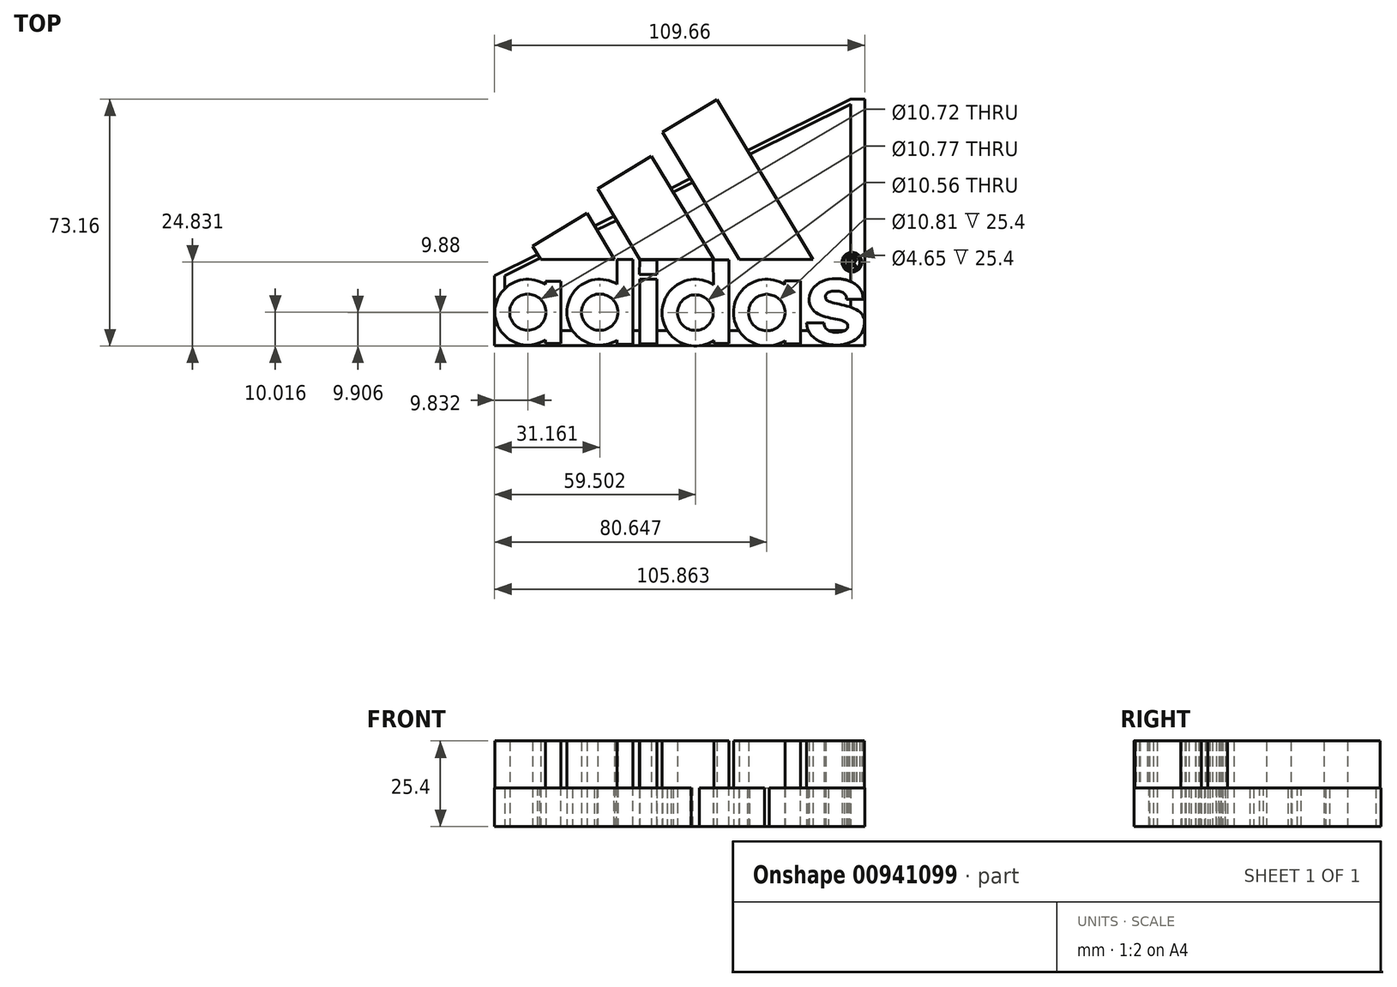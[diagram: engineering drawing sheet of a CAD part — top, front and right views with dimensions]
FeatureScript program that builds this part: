
annotation { "Feature Type Name" : "Feature", "Feature Type Description" : "" }
export const myFeature = defineFeature(function(context is Context, id is Id, definition is map)
    precondition{}
    {
        {
            var Q0;
            Q0=qCreatedBy(makeId("Top.planeOp"),FACE);
            var sketch = newSketch(context, id + "F0", { "sketchPlane" : qUnion([Q0])});
            skLineSegment(sketch, "E0", {"start": v(-48.12, -6.63) * mm, "end": v(-45.76, -10.62) * mm});
            skLineSegment(sketch, "E1", {"start": v(-45.76, -10.62) * mm, "end": v(-23.92, -10.62) * mm});
            skLineSegment(sketch, "E2", {"start": v(-23.92, -10.62) * mm, "end": v(-32.06, 3.04) * mm});
            skLineSegment(sketch, "E3", {"start": v(-32.06, 3.04) * mm, "end": v(-48.12, -6.63) * mm});
            skLineSegment(sketch, "E4", {"start": v(-28.86, 10.33) * mm, "end": v(-16.43, -10.57) * mm});
            skLineSegment(sketch, "E5", {"start": v(-16.43, -10.57) * mm, "end": v(5.51, -10.57) * mm});
            skLineSegment(sketch, "E6", {"start": v(5.51, -10.57) * mm, "end": v(-12.92, 20) * mm});
            skLineSegment(sketch, "E7", {"start": v(-12.92, 20) * mm, "end": v(-28.86, 10.33) * mm});
            skLineSegment(sketch, "E8", {"start": v(13, -10.63) * mm, "end": v(34.92, -10.63) * mm});
            skLineSegment(sketch, "E9", {"start": v(34.92, -10.63) * mm, "end": v(6.4, 36.7) * mm});
            skLineSegment(sketch, "E10", {"start": v(6.4, 36.7) * mm, "end": v(-9.65, 27.04) * mm});
            skLineSegment(sketch, "E11", {"start": v(-9.65, 27.04) * mm, "end": v(13, -10.63) * mm});
            skLineSegment(sketch, "E12", {"start": v(-44.36, -17.06) * mm, "end": v(-39.82, -17.06) * mm});
            skLineSegment(sketch, "E13", {"start": v(-39.82, -17.06) * mm, "end": v(-39.82, -35.56) * mm});
            skLineSegment(sketch, "E14", {"start": v(-39.82, -35.56) * mm, "end": v(-44.36, -35.56) * mm});
            skLineSegment(sketch, "E15", {"start": v(-23.11, -10.57) * mm, "end": v(-18.48, -10.57) * mm});
            skLineSegment(sketch, "E16", {"start": v(-18.48, -10.57) * mm, "end": v(-18.48, -35.72) * mm});
            skLineSegment(sketch, "E17", {"start": v(-18.48, -35.72) * mm, "end": v(-23.07, -35.72) * mm});
            skCircle(sketch, "E18", {"center": v(-49.58, -26.25) * mm, "radius": 9.74 * mm});
            skCircle(sketch, "E19", {"center": v(-28.25, -26.25) * mm, "radius": 9.75 * mm});
            skCircle(sketch, "E20", {"center": v(0.1, -26.39) * mm, "radius": 9.88 * mm});
            skCircle(sketch, "E21", {"center": v(21.24, -26.36) * mm, "radius": 9.86 * mm});
            skLineSegment(sketch, "E22", {"start": v(-16.48, -15.1) * mm, "end": v(-11.34, -15.1) * mm});
            skLineSegment(sketch, "E23", {"start": v(-11.34, -15.1) * mm, "end": v(-11.34, -10.8) * mm});
            skLineSegment(sketch, "E24", {"start": v(-11.34, -10.8) * mm, "end": v(-16.45, -10.8) * mm});
            skLineSegment(sketch, "E25", {"start": v(-16.45, -10.8) * mm, "end": v(-16.48, -15.1) * mm});
            skLineSegment(sketch, "E26", {"start": v(-16.37, -16.5) * mm, "end": v(-11.37, -16.5) * mm});
            skLineSegment(sketch, "E27", {"start": v(-11.37, -16.5) * mm, "end": v(-11.37, -35.62) * mm});
            skLineSegment(sketch, "E28", {"start": v(-11.37, -35.62) * mm, "end": v(-16.35, -35.62) * mm});
            skLineSegment(sketch, "E29", {"start": v(-16.35, -35.62) * mm, "end": v(-16.37, -16.5) * mm});
            skLineSegment(sketch, "E30", {"start": v(5.37, -10.76) * mm, "end": v(10.03, -10.76) * mm});
            skLineSegment(sketch, "E31", {"start": v(10.03, -10.76) * mm, "end": v(10.03, -35.57) * mm});
            skLineSegment(sketch, "E32", {"start": v(10.03, -35.57) * mm, "end": v(5.51, -35.57) * mm});
            skLineSegment(sketch, "E33", {"start": v(26.55, -17.03) * mm, "end": v(31.2, -17.03) * mm});
            skLineSegment(sketch, "E34", {"start": v(31.2, -17.03) * mm, "end": v(31.2, -35.6) * mm});
            skLineSegment(sketch, "E35", {"start": v(31.2, -35.6) * mm, "end": v(26.62, -35.6) * mm});
            skCircle(sketch, "E36", {"center": v(-49.58, -26.25) * mm, "radius": 5.36 * mm});
            skCircle(sketch, "E37", {"center": v(-28.25, -26.25) * mm, "radius": 5.39 * mm});
            skCircle(sketch, "E38", {"center": v(0.1, -26.39) * mm, "radius": 5.28 * mm});
            skCircle(sketch, "E39", {"center": v(21.24, -26.36) * mm, "radius": 5.4 * mm});
            skLineSegment(sketch, "E40", {"start": v(-44.36, -35.56) * mm, "end": v(-44.36, -17.06) * mm});
            skLineSegment(sketch, "E41", {"start": v(-23.07, -35.72) * mm, "end": v(-23.11, -10.57) * mm});
            skLineSegment(sketch, "E42", {"start": v(5.51, -35.57) * mm, "end": v(5.37, -10.76) * mm});
            skLineSegment(sketch, "E43", {"start": v(26.55, -17.03) * mm, "end": v(26.62, -35.6) * mm});
            skCircle(sketch, "E44", {"center": v(46.45, -11.44) * mm, "radius": 2.92 * mm});
            skCircle(sketch, "E45", {"center": v(46.45, -11.44) * mm, "radius": 2.33 * mm});
            skFitSpline(sketch, "E46", {"points": [v(49.72, -22.41) * mm, v(33.72, -22.3) * mm], "startDerivative": vector(1.34, 22.95) * mm, "endDerivative": vector(-2.06, -25.44) * mm});
            skFitSpline(sketch, "E47", {"points": [v(33.72, -22.3) * mm, v(45.18, -30.56) * mm], "startDerivative": vector(0.87, -23.1) * mm, "endDerivative": vector(-1.17, -11.35) * mm});
            skFitSpline(sketch, "E48", {"points": [v(38.16, -29.4) * mm, v(45.18, -30.56) * mm], "startDerivative": vector(0.07, -12.28) * mm, "endDerivative": vector(-0.36, 5.8) * mm});
            skFitSpline(sketch, "E49", {"points": [v(33.03, -29.41) * mm, v(50.17, -29.38) * mm], "startDerivative": vector(0.17, -25.21) * mm, "endDerivative": vector(0.56, 27.5) * mm});
            skFitSpline(sketch, "E50", {"points": [v(50.17, -29.38) * mm, v(38.67, -22.07) * mm], "startDerivative": vector(0.52, 18.6) * mm, "endDerivative": vector(-0.45, 7.35) * mm});
            skFitSpline(sketch, "E51", {"points": [v(38.67, -22.07) * mm, v(44.77, -22.07) * mm], "startDerivative": vector(-2.36, 8.49) * mm, "endDerivative": vector(-0.86, -8.34) * mm});
            skLineSegment(sketch, "E52", {"start": v(33.03, -29.41) * mm, "end": v(38.16, -29.4) * mm});
            skLineSegment(sketch, "E53", {"start": v(49.72, -22.41) * mm, "end": v(44.77, -22.41) * mm});
            skLineSegment(sketch, "E54", {"start": v(44.77, -22.41) * mm, "end": v(44.77, -22.07) * mm});
            skLineSegment(sketch, "E55.bottom", {"start": v(45.7, -13.01) * mm, "end": v(45.16, -13.01) * mm});
            skLineSegment(sketch, "E55.top", {"start": v(45.7, -9.92) * mm, "end": v(45.16, -9.92) * mm});
            skLineSegment(sketch, "E55.left", {"start": v(45.7, -13.01) * mm, "end": v(45.7, -9.92) * mm});
            skLineSegment(sketch, "E55.right", {"start": v(45.16, -13.01) * mm, "end": v(45.16, -9.92) * mm});
            skLineSegment(sketch, "E56", {"start": v(45.7, -9.92) * mm, "end": v(47.02, -9.92) * mm});
            skLineSegment(sketch, "E57", {"start": v(45.7, -11.78) * mm, "end": v(46.41, -11.78) * mm});
            skLineSegment(sketch, "E58", {"start": v(46.41, -11.78) * mm, "end": v(47.15, -12.94) * mm});
            skLineSegment(sketch, "E59", {"start": v(47.15, -12.94) * mm, "end": v(47.85, -12.94) * mm});
            skLineSegment(sketch, "E60", {"start": v(47.85, -12.94) * mm, "end": v(47.05, -11.78) * mm});
            skLineSegment(sketch, "E61", {"start": v(47.05, -11.78) * mm, "end": v(46.83, -11.78) * mm});
            skFitSpline(sketch, "E62", {"points": [v(46.83, -11.78) * mm, v(47.02, -9.92) * mm], "startDerivative": vector(-0.66, 0.48) * mm, "endDerivative": vector(-5.18, 3.5) * mm});
            skLineSegment(sketch, "E63", {"start": v(45.7, -10.48) * mm, "end": v(46.8, -10.48) * mm});
            skLineSegment(sketch, "E64", {"start": v(45.7, -11.11) * mm, "end": v(46.8, -11.11) * mm});
            skFitSpline(sketch, "E65", {"points": [v(46.8, -10.48) * mm, v(46.8, -11.11) * mm], "startDerivative": vector(1.32, -1.07) * mm, "endDerivative": vector(-0.32, -0.18) * mm});
            skSolve(sketch);
        }
        {
            var Q0;
            {var subQ0=sQuery(id+"F0.wireOp",EDGE,"E40");var subQ1=sQuery(id+"F0.wireOp",EDGE,"E18");var subQ2=makeQuery(id+"F0.imprint","INTERSECT",VERTEX,{"disambiguationData":[OD(0.0)],"derivedFrom":[subQ1,subQ0]});Q0=makeQuery(id+"F0.imprint","IMPRINT",FACE,{"disambiguationData":[TD([[makeQuery(id+"F0.imprint","IMPRINT",EDGE,{"disambiguationData":[TD([[subQ2,1.0]])],"derivedFrom":subQ1}),1.0]])]});}
            var Q1;
            {var subQ0=sQuery(id+"F0.wireOp",EDGE,"E40");var subQ1=sQuery(id+"F0.wireOp",EDGE,"E18");var subQ2=makeQuery(id+"F0.imprint","INTERSECT",VERTEX,{"disambiguationData":[OD(0.0)],"derivedFrom":[subQ1,subQ0]});Q1=makeQuery(id+"F0.imprint","IMPRINT",FACE,{"disambiguationData":[TD([[makeQuery(id+"F0.imprint","IMPRINT",EDGE,{"disambiguationData":[TD([[subQ2,-1.0]])],"derivedFrom":subQ1}),1.0]])]});}
            var Q2;
            {var subQ5=sQuery(id+"F0.wireOp",EDGE,"E12");Q2=makeQuery(id+"F0.imprint","IMPRINT",FACE,{"disambiguationData":[TD([[makeQuery(id+"F0.imprint","IMPRINT",EDGE,{"derivedFrom":subQ5}),-1.0]])]});}
            var Q3;
            {var subQ0=sQuery(id+"F0.wireOp",EDGE,"E41");var subQ1=sQuery(id+"F0.wireOp",EDGE,"E19");var subQ2=makeQuery(id+"F0.imprint","INTERSECT",VERTEX,{"disambiguationData":[OD(0.0)],"derivedFrom":[subQ1,subQ0]});Q3=makeQuery(id+"F0.imprint","IMPRINT",FACE,{"disambiguationData":[TD([[makeQuery(id+"F0.imprint","IMPRINT",EDGE,{"disambiguationData":[TD([[subQ2,1.0]])],"derivedFrom":subQ1}),1.0]])]});}
            var Q4;
            {var subQ0=sQuery(id+"F0.wireOp",EDGE,"E41");var subQ1=sQuery(id+"F0.wireOp",EDGE,"E19");var subQ2=makeQuery(id+"F0.imprint","INTERSECT",VERTEX,{"disambiguationData":[OD(0.0)],"derivedFrom":[subQ1,subQ0]});Q4=makeQuery(id+"F0.imprint","IMPRINT",FACE,{"disambiguationData":[TD([[makeQuery(id+"F0.imprint","IMPRINT",EDGE,{"disambiguationData":[TD([[subQ2,-1.0]])],"derivedFrom":subQ1}),1.0]])]});}
            var Q5;
            {var subQ5=sQuery(id+"F0.wireOp",EDGE,"E15");Q5=makeQuery(id+"F0.imprint","IMPRINT",FACE,{"disambiguationData":[TD([[makeQuery(id+"F0.imprint","IMPRINT",EDGE,{"derivedFrom":subQ5}),-1.0]])]});}
            var Q6;
            Q6=makeQuery(id+"F0.imprint","IMPRINT",FACE,{"disambiguationData":[TD([[makeQuery(id+"F0.imprint","IMPRINT",EDGE,{"derivedFrom":sQuery(id+"F0.wireOp",EDGE,"E26")}),-1.0]])]});
            var Q7;
            Q7=makeQuery(id+"F0.imprint","IMPRINT",FACE,{"disambiguationData":[TD([[makeQuery(id+"F0.imprint","IMPRINT",EDGE,{"derivedFrom":sQuery(id+"F0.wireOp",EDGE,"E22")}),1.0]])]});
            var Q8;
            Q8=makeQuery(id+"F0.imprint","IMPRINT",FACE,{"disambiguationData":[TD([[makeQuery(id+"F0.imprint","IMPRINT",EDGE,{"derivedFrom":sQuery(id+"F0.wireOp",EDGE,"E38")}),-1.0]])]});
            var Q9;
            {var subQ0=sQuery(id+"F0.wireOp",EDGE,"E42");var subQ1=sQuery(id+"F0.wireOp",EDGE,"E20");var subQ2=makeQuery(id+"F0.imprint","INTERSECT",VERTEX,{"disambiguationData":[OD(0.0)],"derivedFrom":[subQ1,subQ0]});Q9=makeQuery(id+"F0.imprint","IMPRINT",FACE,{"disambiguationData":[TD([[makeQuery(id+"F0.imprint","IMPRINT",EDGE,{"disambiguationData":[TD([[subQ2,-1.0]])],"derivedFrom":subQ1}),1.0]])]});}
            var Q10;
            {var subQ4=sQuery(id+"F0.wireOp",EDGE,"E30");Q10=makeQuery(id+"F0.imprint","IMPRINT",FACE,{"disambiguationData":[TD([[makeQuery(id+"F0.imprint","IMPRINT",EDGE,{"derivedFrom":subQ4}),-1.0]])]});}
            var Q11;
            {var subQ0=sQuery(id+"F0.wireOp",EDGE,"E43");var subQ1=sQuery(id+"F0.wireOp",EDGE,"E21");var subQ2=makeQuery(id+"F0.imprint","INTERSECT",VERTEX,{"disambiguationData":[OD(0.0)],"derivedFrom":[subQ1,subQ0]});Q11=makeQuery(id+"F0.imprint","IMPRINT",FACE,{"disambiguationData":[TD([[makeQuery(id+"F0.imprint","IMPRINT",EDGE,{"disambiguationData":[TD([[subQ2,-1.0]])],"derivedFrom":subQ1}),1.0]])]});}
            var Q12;
            {var subQ0=sQuery(id+"F0.wireOp",EDGE,"E43");var subQ1=sQuery(id+"F0.wireOp",EDGE,"E21");var subQ2=makeQuery(id+"F0.imprint","INTERSECT",VERTEX,{"disambiguationData":[OD(0.0)],"derivedFrom":[subQ1,subQ0]});Q12=makeQuery(id+"F0.imprint","IMPRINT",FACE,{"disambiguationData":[TD([[makeQuery(id+"F0.imprint","IMPRINT",EDGE,{"disambiguationData":[TD([[subQ2,1.0]])],"derivedFrom":subQ1}),1.0]])]});}
            var Q13;
            {var subQ2=sQuery(id+"F0.wireOp",EDGE,"E33");Q13=makeQuery(id+"F0.imprint","IMPRINT",FACE,{"disambiguationData":[TD([[makeQuery(id+"F0.imprint","IMPRINT",EDGE,{"derivedFrom":subQ2}),-1.0]])]});}
            var Q14;
            Q14=makeQuery(id+"F0.imprint","IMPRINT",FACE,{"disambiguationData":[TD([[makeQuery(id+"F0.imprint","IMPRINT",EDGE,{"derivedFrom":sQuery(id+"F0.wireOp",EDGE,"E46")}),1.0]])]});
            var Q15;
            Q15=makeQuery(id+"F0.imprint","IMPRINT",FACE,{"disambiguationData":[TD([[makeQuery(id+"F0.imprint","IMPRINT",EDGE,{"derivedFrom":sQuery(id+"F0.wireOp",EDGE,"E0")}),1.0]])]});
            var Q16;
            Q16=makeQuery(id+"F0.imprint","IMPRINT",FACE,{"disambiguationData":[TD([[makeQuery(id+"F0.imprint","IMPRINT",EDGE,{"derivedFrom":sQuery(id+"F0.wireOp",EDGE,"E4")}),1.0]])]});
            var Q17;
            Q17=makeQuery(id+"F0.imprint","IMPRINT",FACE,{"disambiguationData":[TD([[makeQuery(id+"F0.imprint","IMPRINT",EDGE,{"derivedFrom":sQuery(id+"F0.wireOp",EDGE,"E8")}),1.0]])]});
            var Q18;
            Q18=makeQuery(id+"F0.imprint","IMPRINT",FACE,{"disambiguationData":[TD([[makeQuery(id+"F0.imprint","IMPRINT",EDGE,{"derivedFrom":sQuery(id+"F0.wireOp",EDGE,"E44")}),1.0]])]});
            var Q19;
            {var subQ3=sQuery(id+"F0.wireOp",EDGE,"E55.bottom");Q19=makeQuery(id+"F0.imprint","IMPRINT",FACE,{"disambiguationData":[TD([[makeQuery(id+"F0.imprint","IMPRINT",EDGE,{"derivedFrom":subQ3}),-1.0]])]});}
            var Q20;
            {var subQ4=sQuery(id+"F0.wireOp",EDGE,"E56");Q20=makeQuery(id+"F0.imprint","IMPRINT",FACE,{"disambiguationData":[TD([[makeQuery(id+"F0.imprint","IMPRINT",EDGE,{"derivedFrom":subQ4}),-1.0]])]});}
            extrude(context, id + "F1", {"entities" : qUnion([Q0, Q1, Q2, Q3, Q4, Q5, Q6, Q7, Q8, Q9, Q10, Q11, Q12, Q13, Q14, Q15, Q16, Q17, Q18, Q19, Q20]), "depth" : 25.4 * mm, "offsetDistance" : 25.4 * mm});
        }
        {
            var Q0;
            Q0=qCreatedBy(makeId("Top.planeOp"),FACE);
            var sketch = newSketch(context, id + "F2", { "sketchPlane" : qUnion([Q0])});
            skLineSegment(sketch, "E66.bottom", {"start": v(-59.4, -31.72) * mm, "end": v(50.25, -31.72) * mm});
            skLineSegment(sketch, "E66.top", {"start": v(-59.4, -36.2) * mm, "end": v(50.25, -36.2) * mm});
            skLineSegment(sketch, "E66.left", {"start": v(-59.4, -31.72) * mm, "end": v(-59.4, -36.2) * mm});
            skLineSegment(sketch, "E66.right", {"start": v(50.25, -31.72) * mm, "end": v(50.25, -36.2) * mm});
            skLineSegment(sketch, "E67.bottom", {"start": v(-59.4, -31.72) * mm, "end": v(-56.38, -31.72) * mm});
            skLineSegment(sketch, "E67.top", {"start": v(-59.4, -15.42) * mm, "end": v(-56.38, -15.42) * mm});
            skLineSegment(sketch, "E67.left", {"start": v(-59.4, -31.72) * mm, "end": v(-59.4, -15.42) * mm});
            skLineSegment(sketch, "E67.right", {"start": v(-56.38, -31.72) * mm, "end": v(-56.38, -15.42) * mm});
            skLineSegment(sketch, "E68.bottom", {"start": v(50.25, -31.72) * mm, "end": v(46.1, -31.72) * mm});
            skLineSegment(sketch, "E68.top", {"start": v(50.25, 36.9) * mm, "end": v(46.1, 36.9) * mm});
            skLineSegment(sketch, "E68.left", {"start": v(50.25, -31.72) * mm, "end": v(50.25, 36.9) * mm});
            skLineSegment(sketch, "E68.right", {"start": v(46.1, -31.72) * mm, "end": v(46.1, 36.9) * mm});
            skLineSegment(sketch, "E69", {"start": v(-59.4, -15.42) * mm, "end": v(46.1, 36.9) * mm});
            skLineSegment(sketch, "E70", {"start": v(-56.38, -15.42) * mm, "end": v(46.1, 35.4) * mm});
            skLineSegment(sketch, "E71.bottom", {"start": v(-16.29, 4.46) * mm, "end": v(-10.93, 4.46) * mm});
            skLineSegment(sketch, "E71.top", {"start": v(-16.29, -31.72) * mm, "end": v(-10.93, -31.72) * mm});
            skLineSegment(sketch, "E71.left", {"start": v(-16.29, 4.46) * mm, "end": v(-16.29, -31.72) * mm});
            skLineSegment(sketch, "E71.right", {"start": v(-10.93, 4.46) * mm, "end": v(-10.93, -31.72) * mm});
            skSolve(sketch);
        }
        {
            var Q0;
            {var subQ5=sQuery(id+"F2.wireOp",EDGE,"E67.top");Q0=makeQuery(id+"F2.imprint","IMPRINT",FACE,{"disambiguationData":[TD([[makeQuery(id+"F2.imprint","IMPRINT",EDGE,{"derivedFrom":subQ5}),1.0]])]});}
            var Q1;
            {var subQ1=sQuery(id+"F2.wireOp",EDGE,"E68.top");Q1=makeQuery(id+"F2.imprint","IMPRINT",FACE,{"disambiguationData":[TD([[makeQuery(id+"F2.imprint","IMPRINT",EDGE,{"derivedFrom":subQ1}),1.0]])]});}
            var Q2;
            Q2=makeQuery(id+"F2.imprint","IMPRINT",FACE,{"disambiguationData":[TD([[makeQuery(id+"F2.imprint","IMPRINT",EDGE,{"derivedFrom":sQuery(id+"F2.wireOp",EDGE,"E66.top")}),1.0]])]});
            var Q3;
            Q3=makeQuery(id+"F2.imprint","IMPRINT",FACE,{"disambiguationData":[TD([[makeQuery(id+"F2.imprint","IMPRINT",EDGE,{"derivedFrom":sQuery(id+"F2.wireOp",EDGE,"E67.top")}),-1.0]])]});
            extrude(context, id + "F3", {"entities" : qUnion([Q0, Q1, Q2, Q3]), "operationType" : NewBodyOperationType.ADD, "depth" : 11.43 * mm, "offsetDistance" : 25.4 * mm});
        }
    });
